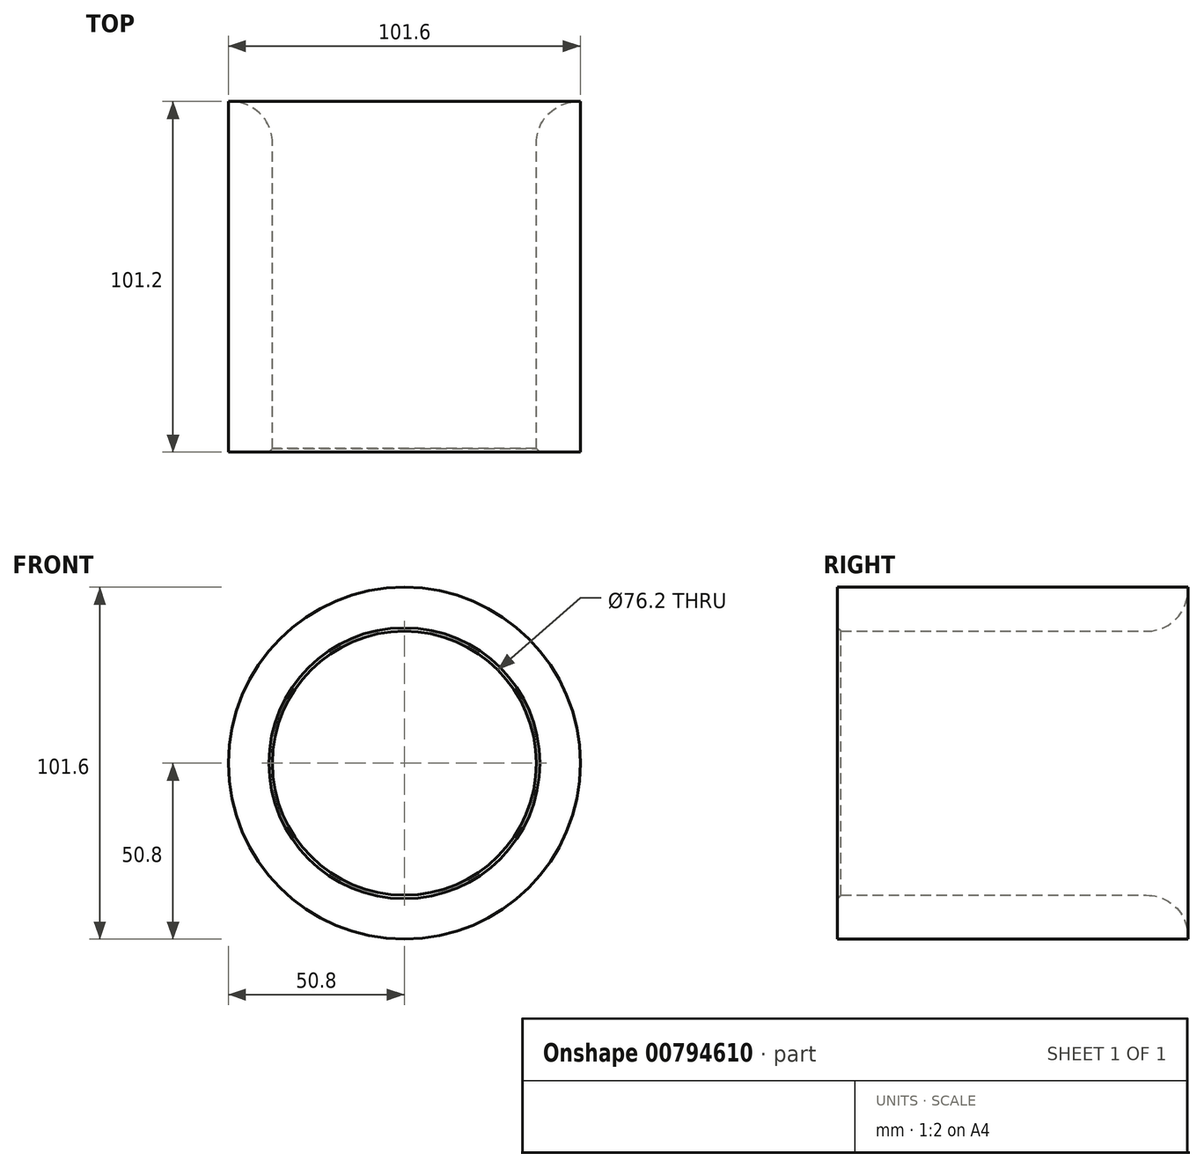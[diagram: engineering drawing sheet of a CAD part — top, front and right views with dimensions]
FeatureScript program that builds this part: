
annotation { "Feature Type Name" : "Feature", "Feature Type Description" : "" }
export const myFeature = defineFeature(function(context is Context, id is Id, definition is map)
    precondition{}
    {
        {
            var Q0;
            Q0=qCreatedBy(makeId("Front.planeOp"),FACE);
            var sketch = newSketch(context, id + "F0", { "sketchPlane" : qUnion([Q0])});
            skCircle(sketch, "E0", {"center": v(0, 0) * mm, "radius": 38.1 * mm});
            skCircle(sketch, "E1", {"center": v(0, 0) * mm, "radius": 50.8 * mm});
            skSolve(sketch);
        }
        {
            var Q0;
            Q0 = qSketchRegion(id + "F0", true);
            extrude(context, id + "F1", {"entities" : qUnion([Q0]), "depth" : 101.2 * mm, "offsetDistance" : 25 * mm});
        }
        {
            var Q0;
            Q0=makeQuery(id+"F1.opExtrude","CAP_EDGE",EDGE,{"disambiguationData":[OSD([sQuery(id+"F0.wireOp",EDGE,"E0")])],"isStart":true});
            fillet(context, id + "F2", {"entities" : qUnion([Q0]), "radius" : 12 * mm, "tangentPropagation" : true, "allowEdgeOverflow" : false});
        }
        {
            var Q0;
            Q0=makeQuery(id+"F1.opExtrude","SWEPT_FACE",FACE,{"disambiguationData":[OSD([sQuery(id+"F0.wireOp",EDGE,"E0")])]});
            var Q1;
            Q1=makeQuery(id+"FayTNMk1r0rX5KJ_1.hole-0.boolean.opBoolean","INTERSECT",EDGE,{"derivedFrom":[makeQuery(id+"FgDWXCsq90Ce0yp_1.opExtrude","CAP_FACE",FACE,{"disambiguationData":[OSD([sQuery(id+"Fzmzgbb1CQ5pxpr_1.wireOp",EDGE,"qn9zq4F6-ZHbD-6NJt-HCxR-mtGEbxXzJJ3Y"),sQuery(id+"Fzmzgbb1CQ5pxpr_1.wireOp",EDGE,"WwQzuDB6-xSEX-ROF9-pkOd-nudWZDl8074e"),sQuery(id+"Fzmzgbb1CQ5pxpr_1.wireOp",EDGE,"NtMjrK89-Q3Fk-pQxf-LzA4-fs9uGENbq9AI"),sQuery(id+"Fzmzgbb1CQ5pxpr_1.wireOp",EDGE,"irWDcrm5-Cc2u-YslT-LI9I-Ugq4cfA6c07y")])],"isStart":false}),makeQuery(id+"FayTNMk1r0rX5KJ_1.hole-0.opRevolve","SWEPT_FACE",FACE,{"disambiguationData":[OSD([sQuery(id+"FayTNMk1r0rX5KJ_1.hole-0.sketch.wireOp",EDGE,"core_line_2")])]})]});
            var Q2;
            Q2=makeQuery(id+"FayTNMk1r0rX5KJ_1.hole-0.boolean.opBoolean","COPY",EDGE,{"derivedFrom":makeQuery(id+"FayTNMk1r0rX5KJ_1.hole-0.opRevolve","SWEPT_EDGE",EDGE,{"disambiguationData":[OSD([sQuery(id+"FayTNMk1r0rX5KJ_1.hole-0.sketch.wireOp",EDGE,"core_line_2"),sQuery(id+"FayTNMk1r0rX5KJ_1.hole-0.sketch.wireOp",EDGE,"core_line_3")])]})});
            chamfer(context, id + "F3", {"entities" : qUnion([Q0, Q1, Q2]), "width" : 1 * mm, "tangentPropagation" : true});
        }
    });
